# Revit family: Maxlogic Intelligent Addressable Smoke Damper Control Panel (8 Inputs - 8 Outputs)
name_source: partatom
category: Fire Alarm Devices
units: mm (PartAtom-declared; Revit-internal decimal feet)

## family parameters
Cut with Voids When Loaded = No
Host = Face
Maintain Annotation Orientation = Yes
OmniClass Number = 23.85.30.21
OmniClass Title = Environmental Detection/Registration
Part Type = Normal
Room Calculation Point = No
Round Connector Dimension = Use Diameter
Shared = No

## types (3) — shared parameters
Battery = 2 X (12V DC 7 Ah )
Code Performance = EN 54-4 / EN 54-18
Color = White
Device Adress Setup = The address is given to devices by addressable programmer
External supply = 220 V AC
Fax Number = (+)90 216 466 45 10
Installation Manual = https://mavilielektronik.com
Main Material = Metal Grey
Manufacturer = Mavili Elektronik Ticaret A.Ş.
Model = Maxlogic
Mounting surface = Wall mount
Nominal Depth = 100 mm
Nominal Height = 300 mm
Nominal Width = 400 mm
Operating temperature = (-10°C) - (+55°C)
Operating voltage range = 18-33V/DC
Operatonal Voltage (default) = 24 V/DC
Secondary Material = White Plastic ABS
URL = https://www.mavili.com.tr
Warranty Duration Labor = 2
Warranty Duration Parts = 2
Warranty Duration Unit = Year
zero-valued in all types: Cost, Default Elevation

## per-type parameters (varying)
| type | Description | Product Code | Toggle swıtch |
| Maxlogic Intelligent Addressable 16 way I/O panel (8 Inputs/ 8 Outputs) | Intelligent Addressable 16 way I/O panel (8 Inputs/ 8 Outputs) | ML-1353 | No |
| Maxlogic Intelligent addressable (8 inputs / 8 outputs) smoke damper control panel | Intelligent addressable (8 inputs / 8 outputs) smoke damper control panel | ML-1354 | No |
| Maxlogic Intelligent addressable (8 inputs / 8 outputs) smoke damper control panel with toggle switch card | Intelligent addressable (8 inputs / 8 outputs) smoke damper control panel with toggle switch card | ML-1355 | Yes |

## geometry (parser evidence)
native form markers: Sweep x2
no freeform markers — native parametric forms only
